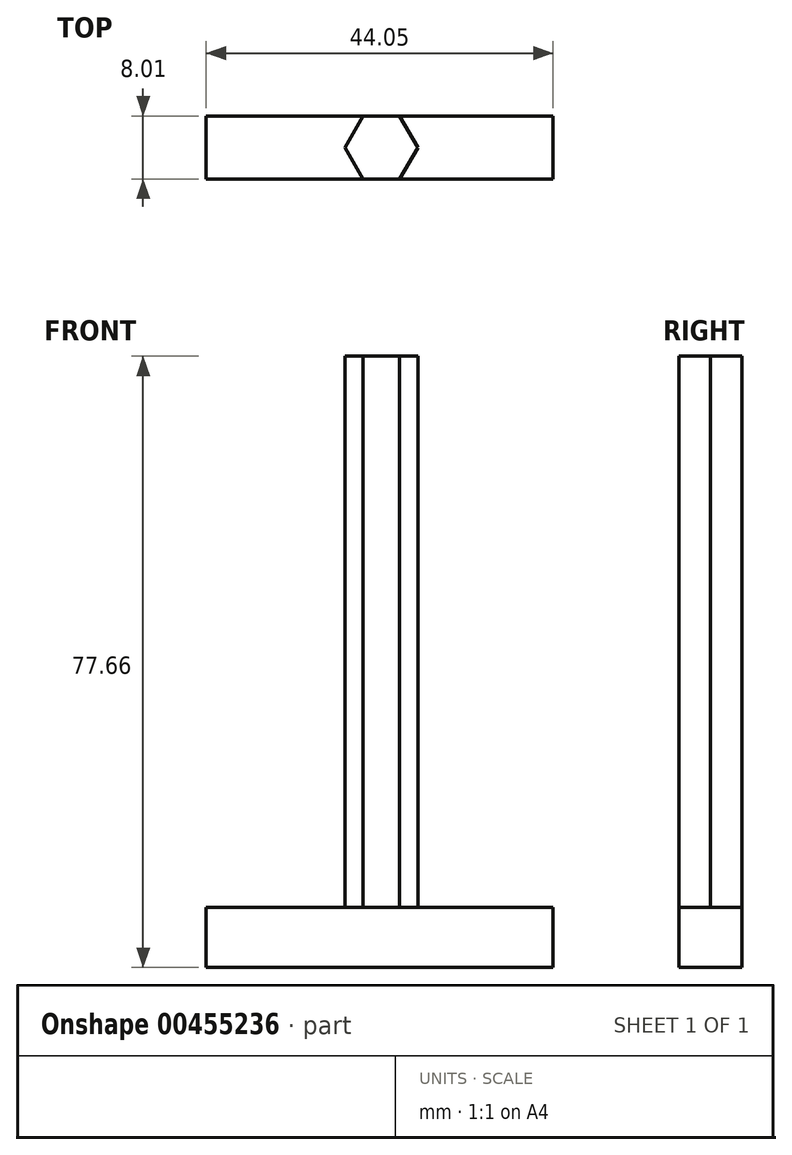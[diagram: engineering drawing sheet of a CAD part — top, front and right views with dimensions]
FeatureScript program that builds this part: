
annotation { "Feature Type Name" : "Feature", "Feature Type Description" : "" }
export const myFeature = defineFeature(function(context is Context, id is Id, definition is map)
    precondition{}
    {
        {
            var Q0;
            Q0=qCreatedBy(makeId("Top.planeOp"),FACE);
            var sketch = newSketch(context, id + "F0", { "sketchPlane" : qUnion([Q0])});
            skCircle(sketch, "E0.cCircle", {"center": v(-3.27, 6.71) * mm, "radius": 4 * mm, "construction": true});
            skLineSegment(sketch, "E0.0", {"start": v(1.35, 6.71) * mm, "end": v(-0.96, 2.71) * mm});
            skLineSegment(sketch, "E0.1", {"start": v(-0.96, 2.71) * mm, "end": v(-5.58, 2.71) * mm});
            skLineSegment(sketch, "E0.2", {"start": v(-5.58, 2.71) * mm, "end": v(-7.89, 6.71) * mm});
            skLineSegment(sketch, "E0.3", {"start": v(-7.89, 6.71) * mm, "end": v(-5.58, 10.71) * mm});
            skLineSegment(sketch, "E0.4", {"start": v(-5.58, 10.71) * mm, "end": v(-0.96, 10.71) * mm});
            skLineSegment(sketch, "E0.5", {"start": v(-0.96, 10.71) * mm, "end": v(1.35, 6.71) * mm});
            skPoint(sketch, "E0.0.midPoint", {"position": v(0.2, 4.71) * mm});
            skSolve(sketch);
        }
        {
            var Q0;
            Q0=makeQuery(id+"F0.imprint","IMPRINT",FACE,{"disambiguationData":[TD([[makeQuery(id+"F0.imprint","IMPRINT",EDGE,{"derivedFrom":sQuery(id+"F0.wireOp",EDGE,"E0.0")}),-1.0]])]});
            extrude(context, id + "F1", {"entities" : qUnion([Q0]), "depth" : 70 * mm});
        }
        {
            var Q0;
            Q0=makeQuery(id+"F1.opExtrude","SWEPT_FACE",FACE,{"disambiguationData":[OSD([sQuery(id+"F0.wireOp",EDGE,"E0.1")])]});
            var sketch = newSketch(context, id + "F2", { "sketchPlane" : qUnion([Q0])});
            skLineSegment(sketch, "E1.bottom", {"start": v(-25.52, 0) * mm, "end": v(18.52, 0) * mm});
            skLineSegment(sketch, "E1.top", {"start": v(-25.52, -7.66) * mm, "end": v(18.52, -7.66) * mm});
            skLineSegment(sketch, "E1.left", {"start": v(-25.52, 0) * mm, "end": v(-25.52, -7.66) * mm});
            skLineSegment(sketch, "E1.right", {"start": v(18.52, 0) * mm, "end": v(18.52, -7.66) * mm});
            skSolve(sketch);
        }
        {
            var Q0;
            Q0=makeQuery(id+"F2.imprint","IMPRINT",FACE,{"disambiguationData":[TD([[makeQuery(id+"F2.imprint","IMPRINT",EDGE,{"derivedFrom":sQuery(id+"F2.wireOp",EDGE,"E1.top")}),1.0]])]});
            extrude(context, id + "F3", {"entities" : qUnion([Q0]), "depth" : -8 * mm});
        }
    });
